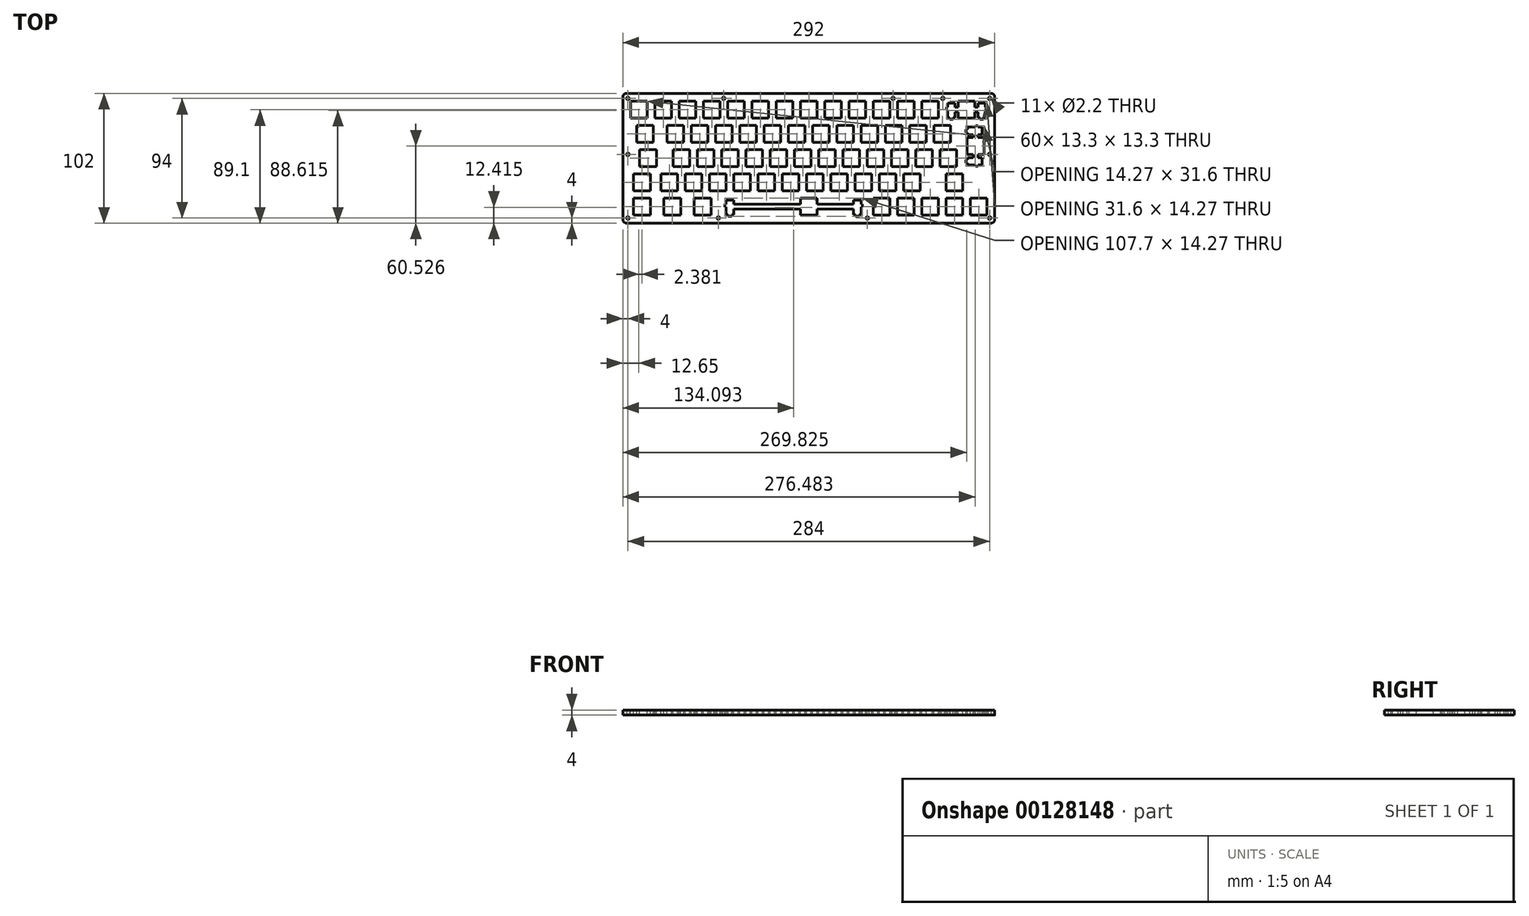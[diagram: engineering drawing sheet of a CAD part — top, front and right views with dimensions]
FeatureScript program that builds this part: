
annotation { "Feature Type Name" : "Feature", "Feature Type Description" : "" }
export const myFeature = defineFeature(function(context is Context, id is Id, definition is map)
    precondition{}
    {
        {
            var Q0;
            Q0=qCreatedBy(makeId("Top.planeOp"),FACE);
            var sketch = newSketch(context, id + "F0", { "sketchPlane" : qUnion([Q0])});
            skLineSegment(sketch, "E0.bottom", {"start": v(-143, 51) * mm, "end": v(143, 51) * mm});
            skLineSegment(sketch, "E0.top", {"start": v(-143, -51) * mm, "end": v(143, -51) * mm});
            skLineSegment(sketch, "E0.left", {"start": v(-146, 48) * mm, "end": v(-146, -48) * mm});
            skLineSegment(sketch, "E0.right", {"start": v(146, 48) * mm, "end": v(146, -48) * mm});
            skPoint(sketch, "E0.middle", {"position": v(0, 0) * mm});
            skPoint(sketch, "E1.visualSharp", {"position": v(-146, 51) * mm});
            skArc(sketch, "E1.filletArc", {"start": v(-143, 51) * mm, "mid": v(-145.12, 50.12) * mm, "end": v(-146, 48) * mm});
            skPoint(sketch, "E2.visualSharp", {"position": v(-146, -51) * mm});
            skArc(sketch, "E2.filletArc", {"start": v(-146, -48) * mm, "mid": v(-145.12, -50.12) * mm, "end": v(-143, -51) * mm});
            skPoint(sketch, "E3.visualSharp", {"position": v(146, 51) * mm});
            skArc(sketch, "E3.filletArc", {"start": v(146, 48) * mm, "mid": v(145.12, 50.12) * mm, "end": v(143, 51) * mm});
            skPoint(sketch, "E4.visualSharp", {"position": v(146, -51) * mm});
            skArc(sketch, "E4.filletArc", {"start": v(143, -51) * mm, "mid": v(145.12, -50.12) * mm, "end": v(146, -48) * mm});
            skCircle(sketch, "E5", {"center": v(-142, 47) * mm, "radius": 1.1 * mm});
            skCircle(sketch, "E6", {"center": v(-66.83, 47) * mm, "radius": 1.1 * mm});
            skCircle(sketch, "E7", {"center": v(66.17, 47) * mm, "radius": 1.1 * mm});
            skCircle(sketch, "E8", {"center": v(105.17, 47) * mm, "radius": 1.1 * mm});
            skCircle(sketch, "E9", {"center": v(142, 47) * mm, "radius": 1.1 * mm});
            skCircle(sketch, "E10", {"center": v(-142, -47) * mm, "radius": 1.1 * mm});
            skCircle(sketch, "E11", {"center": v(142, -47) * mm, "radius": 1.1 * mm});
            skCircle(sketch, "E12", {"center": v(-71, -47) * mm, "radius": 1.1 * mm});
            skCircle(sketch, "E13", {"center": v(46, -47) * mm, "radius": 1.1 * mm});
            skCircle(sketch, "E14", {"center": v(-142, 3) * mm, "radius": 1.1 * mm});
            skCircle(sketch, "E15", {"center": v(142, 3) * mm, "radius": 1.1 * mm});
            skSolve(sketch);
        }
        {
            var Q0;
            Q0=qSketchRegion(id+"F0",true);
            extrude(context, id + "F1", {"entities" : qUnion([Q0]), "depth" : 4 * mm});
        }
        {
            var Q0;
            Q0=makeQuery(id+"F1.opExtrude","CAP_FACE",FACE,{"disambiguationData":[OSD([sQuery(id+"F0.wireOp",EDGE,"E0.bottom"),sQuery(id+"F0.wireOp",EDGE,"E0.top"),sQuery(id+"F0.wireOp",EDGE,"E0.left"),sQuery(id+"F0.wireOp",EDGE,"E0.right"),sQuery(id+"F0.wireOp",EDGE,"E1.filletArc"),sQuery(id+"F0.wireOp",EDGE,"E2.filletArc"),sQuery(id+"F0.wireOp",EDGE,"E3.filletArc"),sQuery(id+"F0.wireOp",EDGE,"E4.filletArc"),sQuery(id+"F0.wireOp",EDGE,"E5"),sQuery(id+"F0.wireOp",EDGE,"E6"),sQuery(id+"F0.wireOp",EDGE,"E7"),sQuery(id+"F0.wireOp",EDGE,"E8"),sQuery(id+"F0.wireOp",EDGE,"E9"),sQuery(id+"F0.wireOp",EDGE,"E10"),sQuery(id+"F0.wireOp",EDGE,"E11"),sQuery(id+"F0.wireOp",EDGE,"E12"),sQuery(id+"F0.wireOp",EDGE,"E13"),sQuery(id+"F0.wireOp",EDGE,"E14"),sQuery(id+"F0.wireOp",EDGE,"E15")])],"isStart":false});
            var sketch = newSketch(context, id + "F2", { "sketchPlane" : qUnion([Q0])});
            skLineSegment(sketch, "E16", {"start": v(-18.56, -36.15) * mm, "end": v(-58.93, -36.15) * mm});
            skLineSegment(sketch, "E17", {"start": v(-58.93, -36.15) * mm, "end": v(-58.93, -32.92) * mm});
            skLineSegment(sketch, "E18", {"start": v(-58.93, -32.92) * mm, "end": v(-64.88, -32.92) * mm});
            skLineSegment(sketch, "E19", {"start": v(-64.88, -32.92) * mm, "end": v(-64.88, -36.15) * mm});
            skLineSegment(sketch, "E20", {"start": v(-64.88, -36.15) * mm, "end": v(-65.76, -36.15) * mm});
            skLineSegment(sketch, "E21", {"start": v(-65.76, -36.15) * mm, "end": v(-65.76, -38.25) * mm});
            skLineSegment(sketch, "E22", {"start": v(-65.76, -38.25) * mm, "end": v(-64.88, -38.25) * mm});
            skLineSegment(sketch, "E23", {"start": v(-64.88, -38.25) * mm, "end": v(-64.88, -44.52) * mm});
            skLineSegment(sketch, "E24", {"start": v(-64.88, -44.52) * mm, "end": v(-63.2, -44.52) * mm});
            skLineSegment(sketch, "E25", {"start": v(-63.2, -44.52) * mm, "end": v(-63.2, -45.72) * mm});
            skLineSegment(sketch, "E26", {"start": v(-63.2, -45.72) * mm, "end": v(-60.6, -45.72) * mm});
            skLineSegment(sketch, "E27", {"start": v(-60.6, -45.72) * mm, "end": v(-60.6, -44.52) * mm});
            skLineSegment(sketch, "E28", {"start": v(-60.6, -44.52) * mm, "end": v(-58.93, -44.52) * mm});
            skLineSegment(sketch, "E29", {"start": v(-58.93, -44.52) * mm, "end": v(-58.93, -40.05) * mm});
            skLineSegment(sketch, "E30", {"start": v(-58.93, -40.05) * mm, "end": v(-18.56, -40.05) * mm});
            skLineSegment(sketch, "E31", {"start": v(6.65, -40.05) * mm, "end": v(35.12, -40.05) * mm});
            skLineSegment(sketch, "E32", {"start": v(35.12, -40.05) * mm, "end": v(35.12, -44.52) * mm});
            skLineSegment(sketch, "E33", {"start": v(35.12, -44.52) * mm, "end": v(36.8, -44.52) * mm});
            skLineSegment(sketch, "E34", {"start": v(36.8, -44.52) * mm, "end": v(36.8, -45.72) * mm});
            skLineSegment(sketch, "E35", {"start": v(36.8, -45.72) * mm, "end": v(39.4, -45.72) * mm});
            skLineSegment(sketch, "E36", {"start": v(39.4, -45.72) * mm, "end": v(39.4, -44.52) * mm});
            skLineSegment(sketch, "E37", {"start": v(39.4, -44.52) * mm, "end": v(41.07, -44.52) * mm});
            skLineSegment(sketch, "E38", {"start": v(41.07, -44.52) * mm, "end": v(41.07, -38.25) * mm});
            skLineSegment(sketch, "E39", {"start": v(41.07, -38.25) * mm, "end": v(41.94, -38.25) * mm});
            skLineSegment(sketch, "E40", {"start": v(41.94, -38.25) * mm, "end": v(41.94, -36.15) * mm});
            skLineSegment(sketch, "E41", {"start": v(41.94, -36.15) * mm, "end": v(41.07, -36.15) * mm});
            skLineSegment(sketch, "E42", {"start": v(41.07, -36.15) * mm, "end": v(41.07, -32.92) * mm});
            skLineSegment(sketch, "E43", {"start": v(41.07, -32.92) * mm, "end": v(35.12, -32.92) * mm});
            skLineSegment(sketch, "E44", {"start": v(35.12, -32.92) * mm, "end": v(35.12, -36.15) * mm});
            skLineSegment(sketch, "E45", {"start": v(35.12, -36.15) * mm, "end": v(6.65, -36.15) * mm});
            skLineSegment(sketch, "E46", {"start": v(-5.26, -31.45) * mm, "end": v(-6.65, -31.45) * mm});
            skLineSegment(sketch, "E47", {"start": v(-137.62, -31.45) * mm, "end": v(-124.32, -31.45) * mm});
            skLineSegment(sketch, "E48", {"start": v(-124.32, -31.45) * mm, "end": v(-124.32, -44.75) * mm});
            skLineSegment(sketch, "E49", {"start": v(-124.32, -44.75) * mm, "end": v(-137.62, -44.75) * mm});
            skLineSegment(sketch, "E50", {"start": v(-137.62, -44.75) * mm, "end": v(-137.62, -31.45) * mm});
            skLineSegment(sketch, "E51", {"start": v(-113.8, -31.45) * mm, "end": v(-100.5, -31.45) * mm});
            skLineSegment(sketch, "E52", {"start": v(-100.5, -31.45) * mm, "end": v(-100.5, -44.75) * mm});
            skLineSegment(sketch, "E53", {"start": v(-100.5, -44.75) * mm, "end": v(-113.8, -44.75) * mm});
            skLineSegment(sketch, "E54", {"start": v(-113.8, -44.75) * mm, "end": v(-113.8, -31.45) * mm});
            skLineSegment(sketch, "E55", {"start": v(-90, -31.45) * mm, "end": v(-76.7, -31.45) * mm});
            skLineSegment(sketch, "E56", {"start": v(-76.7, -31.45) * mm, "end": v(-76.7, -44.75) * mm});
            skLineSegment(sketch, "E57", {"start": v(-76.7, -44.75) * mm, "end": v(-90, -44.75) * mm});
            skLineSegment(sketch, "E58", {"start": v(-90, -44.75) * mm, "end": v(-90, -31.45) * mm});
            skLineSegment(sketch, "E59", {"start": v(50.5, -31.45) * mm, "end": v(63.8, -31.45) * mm});
            skLineSegment(sketch, "E60", {"start": v(63.8, -31.45) * mm, "end": v(63.8, -44.75) * mm});
            skLineSegment(sketch, "E61", {"start": v(63.8, -44.75) * mm, "end": v(50.5, -44.75) * mm});
            skLineSegment(sketch, "E62", {"start": v(50.5, -44.75) * mm, "end": v(50.5, -31.45) * mm});
            skLineSegment(sketch, "E63", {"start": v(69.55, -31.45) * mm, "end": v(82.85, -31.45) * mm});
            skLineSegment(sketch, "E64", {"start": v(82.85, -31.45) * mm, "end": v(82.85, -44.75) * mm});
            skLineSegment(sketch, "E65", {"start": v(82.85, -44.75) * mm, "end": v(69.55, -44.75) * mm});
            skLineSegment(sketch, "E66", {"start": v(69.55, -44.75) * mm, "end": v(69.55, -31.45) * mm});
            skLineSegment(sketch, "E67", {"start": v(88.6, -31.45) * mm, "end": v(101.9, -31.45) * mm});
            skLineSegment(sketch, "E68", {"start": v(101.9, -31.45) * mm, "end": v(101.9, -44.75) * mm});
            skLineSegment(sketch, "E69", {"start": v(101.9, -44.75) * mm, "end": v(88.6, -44.75) * mm});
            skLineSegment(sketch, "E70", {"start": v(88.6, -44.75) * mm, "end": v(88.6, -31.45) * mm});
            skLineSegment(sketch, "E71", {"start": v(107.65, -31.45) * mm, "end": v(120.95, -31.45) * mm});
            skLineSegment(sketch, "E72", {"start": v(120.95, -31.45) * mm, "end": v(120.95, -44.75) * mm});
            skLineSegment(sketch, "E73", {"start": v(120.95, -44.75) * mm, "end": v(107.65, -44.75) * mm});
            skLineSegment(sketch, "E74", {"start": v(107.65, -44.75) * mm, "end": v(107.65, -31.45) * mm});
            skLineSegment(sketch, "E75", {"start": v(126.7, -31.45) * mm, "end": v(140, -31.45) * mm});
            skLineSegment(sketch, "E76", {"start": v(140, -31.45) * mm, "end": v(140, -44.75) * mm});
            skLineSegment(sketch, "E77", {"start": v(140, -44.75) * mm, "end": v(126.7, -44.75) * mm});
            skLineSegment(sketch, "E78", {"start": v(126.7, -44.75) * mm, "end": v(126.7, -31.45) * mm});
            skLineSegment(sketch, "E79", {"start": v(-137.62, -12.4) * mm, "end": v(-124.32, -12.4) * mm});
            skLineSegment(sketch, "E80", {"start": v(-124.32, -12.4) * mm, "end": v(-124.32, -25.7) * mm});
            skLineSegment(sketch, "E81", {"start": v(-124.32, -25.7) * mm, "end": v(-137.62, -25.7) * mm});
            skLineSegment(sketch, "E82", {"start": v(-137.62, -25.7) * mm, "end": v(-137.62, -12.4) * mm});
            skLineSegment(sketch, "E83", {"start": v(-116.19, -12.4) * mm, "end": v(-102.89, -12.4) * mm});
            skLineSegment(sketch, "E84", {"start": v(-102.89, -12.4) * mm, "end": v(-102.89, -25.7) * mm});
            skLineSegment(sketch, "E85", {"start": v(-102.89, -25.7) * mm, "end": v(-116.19, -25.7) * mm});
            skLineSegment(sketch, "E86", {"start": v(-116.19, -25.7) * mm, "end": v(-116.19, -12.4) * mm});
            skLineSegment(sketch, "E87", {"start": v(-97.14, -12.4) * mm, "end": v(-83.84, -12.4) * mm});
            skLineSegment(sketch, "E88", {"start": v(-83.84, -12.4) * mm, "end": v(-83.84, -25.7) * mm});
            skLineSegment(sketch, "E89", {"start": v(-83.84, -25.7) * mm, "end": v(-97.14, -25.7) * mm});
            skLineSegment(sketch, "E90", {"start": v(-97.14, -25.7) * mm, "end": v(-97.14, -12.4) * mm});
            skLineSegment(sketch, "E91", {"start": v(-78.09, -12.4) * mm, "end": v(-64.79, -12.4) * mm});
            skLineSegment(sketch, "E92", {"start": v(-64.79, -12.4) * mm, "end": v(-64.79, -25.7) * mm});
            skLineSegment(sketch, "E93", {"start": v(-64.79, -25.7) * mm, "end": v(-78.09, -25.7) * mm});
            skLineSegment(sketch, "E94", {"start": v(-78.09, -25.7) * mm, "end": v(-78.09, -12.4) * mm});
            skLineSegment(sketch, "E95", {"start": v(-59.04, -12.4) * mm, "end": v(-45.74, -12.4) * mm});
            skLineSegment(sketch, "E96", {"start": v(-45.74, -12.4) * mm, "end": v(-45.74, -25.7) * mm});
            skLineSegment(sketch, "E97", {"start": v(-45.74, -25.7) * mm, "end": v(-59.04, -25.7) * mm});
            skLineSegment(sketch, "E98", {"start": v(-59.04, -25.7) * mm, "end": v(-59.04, -12.4) * mm});
            skLineSegment(sketch, "E99", {"start": v(-39.99, -12.4) * mm, "end": v(-26.69, -12.4) * mm});
            skLineSegment(sketch, "E100", {"start": v(-26.69, -12.4) * mm, "end": v(-26.69, -25.7) * mm});
            skLineSegment(sketch, "E101", {"start": v(-26.69, -25.7) * mm, "end": v(-39.99, -25.7) * mm});
            skLineSegment(sketch, "E102", {"start": v(-39.99, -25.7) * mm, "end": v(-39.99, -12.4) * mm});
            skLineSegment(sketch, "E103", {"start": v(-20.94, -12.4) * mm, "end": v(-7.64, -12.4) * mm});
            skLineSegment(sketch, "E104", {"start": v(-7.64, -12.4) * mm, "end": v(-7.64, -25.7) * mm});
            skLineSegment(sketch, "E105", {"start": v(-7.64, -25.7) * mm, "end": v(-20.94, -25.7) * mm});
            skLineSegment(sketch, "E106", {"start": v(-20.94, -25.7) * mm, "end": v(-20.94, -12.4) * mm});
            skLineSegment(sketch, "E107", {"start": v(-1.89, -12.4) * mm, "end": v(11.41, -12.4) * mm});
            skLineSegment(sketch, "E108", {"start": v(11.41, -12.4) * mm, "end": v(11.41, -25.7) * mm});
            skLineSegment(sketch, "E109", {"start": v(11.41, -25.7) * mm, "end": v(-1.89, -25.7) * mm});
            skLineSegment(sketch, "E110", {"start": v(-1.89, -25.7) * mm, "end": v(-1.89, -12.4) * mm});
            skLineSegment(sketch, "E111", {"start": v(17.16, -12.4) * mm, "end": v(30.46, -12.4) * mm});
            skLineSegment(sketch, "E112", {"start": v(30.46, -12.4) * mm, "end": v(30.46, -25.7) * mm});
            skLineSegment(sketch, "E113", {"start": v(30.46, -25.7) * mm, "end": v(17.16, -25.7) * mm});
            skLineSegment(sketch, "E114", {"start": v(17.16, -25.7) * mm, "end": v(17.16, -12.4) * mm});
            skLineSegment(sketch, "E115", {"start": v(36.21, -12.4) * mm, "end": v(49.51, -12.4) * mm});
            skLineSegment(sketch, "E116", {"start": v(49.51, -12.4) * mm, "end": v(49.51, -25.7) * mm});
            skLineSegment(sketch, "E117", {"start": v(49.51, -25.7) * mm, "end": v(36.21, -25.7) * mm});
            skLineSegment(sketch, "E118", {"start": v(36.21, -25.7) * mm, "end": v(36.21, -12.4) * mm});
            skLineSegment(sketch, "E119", {"start": v(55.26, -12.4) * mm, "end": v(68.56, -12.4) * mm});
            skLineSegment(sketch, "E120", {"start": v(68.56, -12.4) * mm, "end": v(68.56, -25.7) * mm});
            skLineSegment(sketch, "E121", {"start": v(68.56, -25.7) * mm, "end": v(55.26, -25.7) * mm});
            skLineSegment(sketch, "E122", {"start": v(55.26, -25.7) * mm, "end": v(55.26, -12.4) * mm});
            skLineSegment(sketch, "E123", {"start": v(74.31, -12.4) * mm, "end": v(87.61, -12.4) * mm});
            skLineSegment(sketch, "E124", {"start": v(87.61, -12.4) * mm, "end": v(87.61, -25.7) * mm});
            skLineSegment(sketch, "E125", {"start": v(87.61, -25.7) * mm, "end": v(74.31, -25.7) * mm});
            skLineSegment(sketch, "E126", {"start": v(74.31, -25.7) * mm, "end": v(74.31, -12.4) * mm});
            skLineSegment(sketch, "E127", {"start": v(107.65, -12.4) * mm, "end": v(120.95, -12.4) * mm});
            skLineSegment(sketch, "E128", {"start": v(120.95, -12.4) * mm, "end": v(120.95, -25.7) * mm});
            skLineSegment(sketch, "E129", {"start": v(120.95, -25.7) * mm, "end": v(107.65, -25.7) * mm});
            skLineSegment(sketch, "E130", {"start": v(107.65, -25.7) * mm, "end": v(107.65, -12.4) * mm});
            skLineSegment(sketch, "E131", {"start": v(-132.86, 6.65) * mm, "end": v(-119.56, 6.65) * mm});
            skLineSegment(sketch, "E132", {"start": v(-119.56, 6.65) * mm, "end": v(-119.56, -6.65) * mm});
            skLineSegment(sketch, "E133", {"start": v(-119.56, -6.65) * mm, "end": v(-132.86, -6.65) * mm});
            skLineSegment(sketch, "E134", {"start": v(-132.86, -6.65) * mm, "end": v(-132.86, 6.65) * mm});
            skLineSegment(sketch, "E135", {"start": v(-106.66, 6.65) * mm, "end": v(-93.36, 6.65) * mm});
            skLineSegment(sketch, "E136", {"start": v(-93.36, 6.65) * mm, "end": v(-93.36, -6.65) * mm});
            skLineSegment(sketch, "E137", {"start": v(-93.36, -6.65) * mm, "end": v(-106.66, -6.65) * mm});
            skLineSegment(sketch, "E138", {"start": v(-106.66, -6.65) * mm, "end": v(-106.66, 6.65) * mm});
            skLineSegment(sketch, "E139", {"start": v(-87.61, 6.65) * mm, "end": v(-74.31, 6.65) * mm});
            skLineSegment(sketch, "E140", {"start": v(-74.31, 6.65) * mm, "end": v(-74.31, -6.65) * mm});
            skLineSegment(sketch, "E141", {"start": v(-74.31, -6.65) * mm, "end": v(-87.61, -6.65) * mm});
            skLineSegment(sketch, "E142", {"start": v(-87.61, -6.65) * mm, "end": v(-87.61, 6.65) * mm});
            skLineSegment(sketch, "E143", {"start": v(-68.56, 6.65) * mm, "end": v(-55.26, 6.65) * mm});
            skLineSegment(sketch, "E144", {"start": v(-55.26, 6.65) * mm, "end": v(-55.26, -6.65) * mm});
            skLineSegment(sketch, "E145", {"start": v(-55.26, -6.65) * mm, "end": v(-68.56, -6.65) * mm});
            skLineSegment(sketch, "E146", {"start": v(-68.56, -6.65) * mm, "end": v(-68.56, 6.65) * mm});
            skLineSegment(sketch, "E147", {"start": v(-49.51, 6.65) * mm, "end": v(-36.21, 6.65) * mm});
            skLineSegment(sketch, "E148", {"start": v(-36.21, 6.65) * mm, "end": v(-36.21, -6.65) * mm});
            skLineSegment(sketch, "E149", {"start": v(-36.21, -6.65) * mm, "end": v(-49.51, -6.65) * mm});
            skLineSegment(sketch, "E150", {"start": v(-49.51, -6.65) * mm, "end": v(-49.51, 6.65) * mm});
            skLineSegment(sketch, "E151", {"start": v(-30.46, 6.65) * mm, "end": v(-17.16, 6.65) * mm});
            skLineSegment(sketch, "E152", {"start": v(-17.16, 6.65) * mm, "end": v(-17.16, -6.65) * mm});
            skLineSegment(sketch, "E153", {"start": v(-17.16, -6.65) * mm, "end": v(-30.46, -6.65) * mm});
            skLineSegment(sketch, "E154", {"start": v(-30.46, -6.65) * mm, "end": v(-30.46, 6.65) * mm});
            skLineSegment(sketch, "E155", {"start": v(-11.41, 6.65) * mm, "end": v(1.89, 6.65) * mm});
            skLineSegment(sketch, "E156", {"start": v(1.89, 6.65) * mm, "end": v(1.89, -6.65) * mm});
            skLineSegment(sketch, "E157", {"start": v(1.89, -6.65) * mm, "end": v(-11.41, -6.65) * mm});
            skLineSegment(sketch, "E158", {"start": v(-11.41, -6.65) * mm, "end": v(-11.41, 6.65) * mm});
            skLineSegment(sketch, "E159", {"start": v(7.64, 6.65) * mm, "end": v(20.94, 6.65) * mm});
            skLineSegment(sketch, "E160", {"start": v(20.94, 6.65) * mm, "end": v(20.94, -6.65) * mm});
            skLineSegment(sketch, "E161", {"start": v(20.94, -6.65) * mm, "end": v(7.64, -6.65) * mm});
            skLineSegment(sketch, "E162", {"start": v(7.64, -6.65) * mm, "end": v(7.64, 6.65) * mm});
            skLineSegment(sketch, "E163", {"start": v(26.69, 6.65) * mm, "end": v(39.99, 6.65) * mm});
            skLineSegment(sketch, "E164", {"start": v(39.99, 6.65) * mm, "end": v(39.99, -6.65) * mm});
            skLineSegment(sketch, "E165", {"start": v(39.99, -6.65) * mm, "end": v(26.69, -6.65) * mm});
            skLineSegment(sketch, "E166", {"start": v(26.69, -6.65) * mm, "end": v(26.69, 6.65) * mm});
            skLineSegment(sketch, "E167", {"start": v(45.74, 6.65) * mm, "end": v(59.04, 6.65) * mm});
            skLineSegment(sketch, "E168", {"start": v(59.04, 6.65) * mm, "end": v(59.04, -6.65) * mm});
            skLineSegment(sketch, "E169", {"start": v(59.04, -6.65) * mm, "end": v(45.74, -6.65) * mm});
            skLineSegment(sketch, "E170", {"start": v(45.74, -6.65) * mm, "end": v(45.74, 6.65) * mm});
            skLineSegment(sketch, "E171", {"start": v(64.79, 6.65) * mm, "end": v(78.09, 6.65) * mm});
            skLineSegment(sketch, "E172", {"start": v(78.09, 6.65) * mm, "end": v(78.09, -6.65) * mm});
            skLineSegment(sketch, "E173", {"start": v(78.09, -6.65) * mm, "end": v(64.79, -6.65) * mm});
            skLineSegment(sketch, "E174", {"start": v(64.79, -6.65) * mm, "end": v(64.79, 6.65) * mm});
            skLineSegment(sketch, "E175", {"start": v(83.84, 6.65) * mm, "end": v(97.14, 6.65) * mm});
            skLineSegment(sketch, "E176", {"start": v(97.14, 6.65) * mm, "end": v(97.14, -6.65) * mm});
            skLineSegment(sketch, "E177", {"start": v(97.14, -6.65) * mm, "end": v(83.84, -6.65) * mm});
            skLineSegment(sketch, "E178", {"start": v(83.84, -6.65) * mm, "end": v(83.84, 6.65) * mm});
            skLineSegment(sketch, "E179", {"start": v(102.89, 6.65) * mm, "end": v(116.19, 6.65) * mm});
            skLineSegment(sketch, "E180", {"start": v(116.19, 6.65) * mm, "end": v(116.19, -6.65) * mm});
            skLineSegment(sketch, "E181", {"start": v(116.19, -6.65) * mm, "end": v(102.89, -6.65) * mm});
            skLineSegment(sketch, "E182", {"start": v(102.89, -6.65) * mm, "end": v(102.89, 6.65) * mm});
            skLineSegment(sketch, "E183", {"start": v(130.82, 25.33) * mm, "end": v(130.82, 24.45) * mm});
            skLineSegment(sketch, "E184", {"start": v(130.82, 24.45) * mm, "end": v(124.55, 24.45) * mm});
            skLineSegment(sketch, "E185", {"start": v(124.55, 24.45) * mm, "end": v(124.55, 22.78) * mm});
            skLineSegment(sketch, "E186", {"start": v(124.55, 22.78) * mm, "end": v(123.35, 22.78) * mm});
            skLineSegment(sketch, "E187", {"start": v(123.35, 22.78) * mm, "end": v(123.35, 20.17) * mm});
            skLineSegment(sketch, "E188", {"start": v(123.35, 20.17) * mm, "end": v(124.55, 20.17) * mm});
            skLineSegment(sketch, "E189", {"start": v(124.55, 20.17) * mm, "end": v(124.55, 18.5) * mm});
            skLineSegment(sketch, "E190", {"start": v(124.55, 18.5) * mm, "end": v(129.02, 18.5) * mm});
            skLineSegment(sketch, "E191", {"start": v(129.02, 18.5) * mm, "end": v(129.02, 16.18) * mm});
            skLineSegment(sketch, "E192", {"start": v(129.02, 16.18) * mm, "end": v(124.32, 16.18) * mm});
            skLineSegment(sketch, "E193", {"start": v(124.32, 16.18) * mm, "end": v(124.32, 2.88) * mm});
            skLineSegment(sketch, "E194", {"start": v(124.32, 2.88) * mm, "end": v(129.02, 2.88) * mm});
            skLineSegment(sketch, "E195", {"start": v(129.02, 2.88) * mm, "end": v(129.02, 0.55) * mm});
            skLineSegment(sketch, "E196", {"start": v(129.02, 0.55) * mm, "end": v(124.55, 0.55) * mm});
            skLineSegment(sketch, "E197", {"start": v(124.55, 0.55) * mm, "end": v(124.55, -1.12) * mm});
            skLineSegment(sketch, "E198", {"start": v(124.55, -1.12) * mm, "end": v(123.35, -1.12) * mm});
            skLineSegment(sketch, "E199", {"start": v(123.35, -1.12) * mm, "end": v(123.35, -3.72) * mm});
            skLineSegment(sketch, "E200", {"start": v(123.35, -3.72) * mm, "end": v(124.55, -3.72) * mm});
            skLineSegment(sketch, "E201", {"start": v(124.55, -3.72) * mm, "end": v(124.55, -5.4) * mm});
            skLineSegment(sketch, "E202", {"start": v(124.55, -5.4) * mm, "end": v(130.82, -5.4) * mm});
            skLineSegment(sketch, "E203", {"start": v(130.82, -5.4) * mm, "end": v(130.82, -6.27) * mm});
            skLineSegment(sketch, "E204", {"start": v(130.82, -6.27) * mm, "end": v(132.92, -6.27) * mm});
            skLineSegment(sketch, "E205", {"start": v(132.92, -6.27) * mm, "end": v(132.92, -5.4) * mm});
            skLineSegment(sketch, "E206", {"start": v(132.92, -5.4) * mm, "end": v(136.15, -5.4) * mm});
            skLineSegment(sketch, "E207", {"start": v(136.15, -5.4) * mm, "end": v(136.15, 0.55) * mm});
            skLineSegment(sketch, "E208", {"start": v(136.15, 0.55) * mm, "end": v(132.92, 0.55) * mm});
            skLineSegment(sketch, "E209", {"start": v(132.92, 0.55) * mm, "end": v(132.92, 2.88) * mm});
            skLineSegment(sketch, "E210", {"start": v(132.92, 2.88) * mm, "end": v(137.62, 2.88) * mm});
            skLineSegment(sketch, "E211", {"start": v(137.62, 2.88) * mm, "end": v(137.62, 16.18) * mm});
            skLineSegment(sketch, "E212", {"start": v(137.62, 16.18) * mm, "end": v(132.92, 16.18) * mm});
            skLineSegment(sketch, "E213", {"start": v(132.92, 16.18) * mm, "end": v(132.92, 18.5) * mm});
            skLineSegment(sketch, "E214", {"start": v(132.92, 18.5) * mm, "end": v(136.15, 18.5) * mm});
            skLineSegment(sketch, "E215", {"start": v(136.15, 18.5) * mm, "end": v(136.15, 24.45) * mm});
            skLineSegment(sketch, "E216", {"start": v(136.15, 24.45) * mm, "end": v(132.92, 24.45) * mm});
            skLineSegment(sketch, "E217", {"start": v(132.92, 24.45) * mm, "end": v(132.92, 25.33) * mm});
            skLineSegment(sketch, "E218", {"start": v(132.92, 25.33) * mm, "end": v(130.82, 25.33) * mm});
            skLineSegment(sketch, "E219", {"start": v(-135.24, 25.7) * mm, "end": v(-121.94, 25.7) * mm});
            skLineSegment(sketch, "E220", {"start": v(-121.94, 25.7) * mm, "end": v(-121.94, 12.4) * mm});
            skLineSegment(sketch, "E221", {"start": v(-121.94, 12.4) * mm, "end": v(-135.24, 12.4) * mm});
            skLineSegment(sketch, "E222", {"start": v(-135.24, 12.4) * mm, "end": v(-135.24, 25.7) * mm});
            skLineSegment(sketch, "E223", {"start": v(-111.43, 25.7) * mm, "end": v(-98.12, 25.7) * mm});
            skLineSegment(sketch, "E224", {"start": v(-98.12, 25.7) * mm, "end": v(-98.12, 12.4) * mm});
            skLineSegment(sketch, "E225", {"start": v(-98.12, 12.4) * mm, "end": v(-111.43, 12.4) * mm});
            skLineSegment(sketch, "E226", {"start": v(-111.43, 12.4) * mm, "end": v(-111.43, 25.7) * mm});
            skLineSegment(sketch, "E227", {"start": v(-92.38, 25.7) * mm, "end": v(-79.07, 25.7) * mm});
            skLineSegment(sketch, "E228", {"start": v(-79.07, 25.7) * mm, "end": v(-79.07, 12.4) * mm});
            skLineSegment(sketch, "E229", {"start": v(-79.07, 12.4) * mm, "end": v(-92.38, 12.4) * mm});
            skLineSegment(sketch, "E230", {"start": v(-92.38, 12.4) * mm, "end": v(-92.38, 25.7) * mm});
            skLineSegment(sketch, "E231", {"start": v(-73.33, 25.7) * mm, "end": v(-60.02, 25.7) * mm});
            skLineSegment(sketch, "E232", {"start": v(-60.02, 25.7) * mm, "end": v(-60.02, 12.4) * mm});
            skLineSegment(sketch, "E233", {"start": v(-60.02, 12.4) * mm, "end": v(-73.33, 12.4) * mm});
            skLineSegment(sketch, "E234", {"start": v(-73.33, 12.4) * mm, "end": v(-73.33, 25.7) * mm});
            skLineSegment(sketch, "E235", {"start": v(-54.28, 25.7) * mm, "end": v(-40.97, 25.7) * mm});
            skLineSegment(sketch, "E236", {"start": v(-40.97, 25.7) * mm, "end": v(-40.97, 12.4) * mm});
            skLineSegment(sketch, "E237", {"start": v(-40.97, 12.4) * mm, "end": v(-54.28, 12.4) * mm});
            skLineSegment(sketch, "E238", {"start": v(-54.28, 12.4) * mm, "end": v(-54.28, 25.7) * mm});
            skLineSegment(sketch, "E239", {"start": v(-35.23, 25.7) * mm, "end": v(-21.92, 25.7) * mm});
            skLineSegment(sketch, "E240", {"start": v(-21.92, 25.7) * mm, "end": v(-21.92, 12.4) * mm});
            skLineSegment(sketch, "E241", {"start": v(-21.92, 12.4) * mm, "end": v(-35.23, 12.4) * mm});
            skLineSegment(sketch, "E242", {"start": v(-35.23, 12.4) * mm, "end": v(-35.23, 25.7) * mm});
            skLineSegment(sketch, "E243", {"start": v(-16.18, 25.7) * mm, "end": v(-2.87, 25.7) * mm});
            skLineSegment(sketch, "E244", {"start": v(-2.87, 25.7) * mm, "end": v(-2.87, 12.4) * mm});
            skLineSegment(sketch, "E245", {"start": v(-2.87, 12.4) * mm, "end": v(-16.18, 12.4) * mm});
            skLineSegment(sketch, "E246", {"start": v(-16.18, 12.4) * mm, "end": v(-16.18, 25.7) * mm});
            skLineSegment(sketch, "E247", {"start": v(2.87, 25.7) * mm, "end": v(16.18, 25.7) * mm});
            skLineSegment(sketch, "E248", {"start": v(16.18, 25.7) * mm, "end": v(16.18, 12.4) * mm});
            skLineSegment(sketch, "E249", {"start": v(16.18, 12.4) * mm, "end": v(2.87, 12.4) * mm});
            skLineSegment(sketch, "E250", {"start": v(2.87, 12.4) * mm, "end": v(2.87, 25.7) * mm});
            skLineSegment(sketch, "E251", {"start": v(21.92, 25.7) * mm, "end": v(35.23, 25.7) * mm});
            skLineSegment(sketch, "E252", {"start": v(35.23, 25.7) * mm, "end": v(35.23, 12.4) * mm});
            skLineSegment(sketch, "E253", {"start": v(35.23, 12.4) * mm, "end": v(21.92, 12.4) * mm});
            skLineSegment(sketch, "E254", {"start": v(21.92, 12.4) * mm, "end": v(21.92, 25.7) * mm});
            skLineSegment(sketch, "E255", {"start": v(40.97, 25.7) * mm, "end": v(54.28, 25.7) * mm});
            skLineSegment(sketch, "E256", {"start": v(54.28, 25.7) * mm, "end": v(54.28, 12.4) * mm});
            skLineSegment(sketch, "E257", {"start": v(54.28, 12.4) * mm, "end": v(40.97, 12.4) * mm});
            skLineSegment(sketch, "E258", {"start": v(40.97, 12.4) * mm, "end": v(40.97, 25.7) * mm});
            skLineSegment(sketch, "E259", {"start": v(60.02, 25.7) * mm, "end": v(73.33, 25.7) * mm});
            skLineSegment(sketch, "E260", {"start": v(73.33, 25.7) * mm, "end": v(73.33, 12.4) * mm});
            skLineSegment(sketch, "E261", {"start": v(73.33, 12.4) * mm, "end": v(60.02, 12.4) * mm});
            skLineSegment(sketch, "E262", {"start": v(60.02, 12.4) * mm, "end": v(60.02, 25.7) * mm});
            skLineSegment(sketch, "E263", {"start": v(79.07, 25.7) * mm, "end": v(92.38, 25.7) * mm});
            skLineSegment(sketch, "E264", {"start": v(92.38, 25.7) * mm, "end": v(92.38, 12.4) * mm});
            skLineSegment(sketch, "E265", {"start": v(92.38, 12.4) * mm, "end": v(79.07, 12.4) * mm});
            skLineSegment(sketch, "E266", {"start": v(79.07, 12.4) * mm, "end": v(79.07, 25.7) * mm});
            skLineSegment(sketch, "E267", {"start": v(98.12, 25.7) * mm, "end": v(111.42, 25.7) * mm});
            skLineSegment(sketch, "E268", {"start": v(111.42, 25.7) * mm, "end": v(111.42, 12.4) * mm});
            skLineSegment(sketch, "E269", {"start": v(111.42, 12.4) * mm, "end": v(98.12, 12.4) * mm});
            skLineSegment(sketch, "E270", {"start": v(98.12, 12.4) * mm, "end": v(98.12, 25.7) * mm});
            skLineSegment(sketch, "E271", {"start": v(117.17, 44.75) * mm, "end": v(117.17, 40.05) * mm});
            skLineSegment(sketch, "E272", {"start": v(117.17, 40.05) * mm, "end": v(114.85, 40.05) * mm});
            skLineSegment(sketch, "E273", {"start": v(114.85, 40.05) * mm, "end": v(114.85, 43.28) * mm});
            skLineSegment(sketch, "E274", {"start": v(114.85, 43.28) * mm, "end": v(108.9, 43.28) * mm});
            skLineSegment(sketch, "E275", {"start": v(108.9, 43.28) * mm, "end": v(108.9, 40.05) * mm});
            skLineSegment(sketch, "E276", {"start": v(108.9, 40.05) * mm, "end": v(108.02, 40.05) * mm});
            skLineSegment(sketch, "E277", {"start": v(108.02, 40.05) * mm, "end": v(108.02, 37.95) * mm});
            skLineSegment(sketch, "E278", {"start": v(108.02, 37.95) * mm, "end": v(108.9, 37.95) * mm});
            skLineSegment(sketch, "E279", {"start": v(108.9, 37.95) * mm, "end": v(108.9, 31.68) * mm});
            skLineSegment(sketch, "E280", {"start": v(108.9, 31.68) * mm, "end": v(110.58, 31.68) * mm});
            skLineSegment(sketch, "E281", {"start": v(110.58, 31.68) * mm, "end": v(110.58, 30.48) * mm});
            skLineSegment(sketch, "E282", {"start": v(110.58, 30.48) * mm, "end": v(113.17, 30.48) * mm});
            skLineSegment(sketch, "E283", {"start": v(113.17, 30.48) * mm, "end": v(113.17, 31.68) * mm});
            skLineSegment(sketch, "E284", {"start": v(113.17, 31.68) * mm, "end": v(114.85, 31.68) * mm});
            skLineSegment(sketch, "E285", {"start": v(114.85, 31.68) * mm, "end": v(114.85, 36.15) * mm});
            skLineSegment(sketch, "E286", {"start": v(114.85, 36.15) * mm, "end": v(117.17, 36.15) * mm});
            skLineSegment(sketch, "E287", {"start": v(117.17, 36.15) * mm, "end": v(117.17, 31.45) * mm});
            skLineSegment(sketch, "E288", {"start": v(117.17, 31.45) * mm, "end": v(130.48, 31.45) * mm});
            skLineSegment(sketch, "E289", {"start": v(130.48, 31.45) * mm, "end": v(130.48, 36.15) * mm});
            skLineSegment(sketch, "E290", {"start": v(130.48, 36.15) * mm, "end": v(132.8, 36.15) * mm});
            skLineSegment(sketch, "E291", {"start": v(132.8, 36.15) * mm, "end": v(132.8, 31.68) * mm});
            skLineSegment(sketch, "E292", {"start": v(132.8, 31.68) * mm, "end": v(134.47, 31.68) * mm});
            skLineSegment(sketch, "E293", {"start": v(134.47, 31.68) * mm, "end": v(134.47, 30.48) * mm});
            skLineSegment(sketch, "E294", {"start": v(134.47, 30.48) * mm, "end": v(137.07, 30.48) * mm});
            skLineSegment(sketch, "E295", {"start": v(137.07, 30.48) * mm, "end": v(137.07, 31.68) * mm});
            skLineSegment(sketch, "E296", {"start": v(137.07, 31.68) * mm, "end": v(138.75, 31.68) * mm});
            skLineSegment(sketch, "E297", {"start": v(138.75, 31.68) * mm, "end": v(138.75, 37.95) * mm});
            skLineSegment(sketch, "E298", {"start": v(138.75, 37.95) * mm, "end": v(139.63, 37.95) * mm});
            skLineSegment(sketch, "E299", {"start": v(139.63, 37.95) * mm, "end": v(139.63, 40.05) * mm});
            skLineSegment(sketch, "E300", {"start": v(139.63, 40.05) * mm, "end": v(138.75, 40.05) * mm});
            skLineSegment(sketch, "E301", {"start": v(138.75, 40.05) * mm, "end": v(138.75, 43.28) * mm});
            skLineSegment(sketch, "E302", {"start": v(138.75, 43.28) * mm, "end": v(132.8, 43.28) * mm});
            skLineSegment(sketch, "E303", {"start": v(132.8, 43.28) * mm, "end": v(132.8, 40.05) * mm});
            skLineSegment(sketch, "E304", {"start": v(132.8, 40.05) * mm, "end": v(130.48, 40.05) * mm});
            skLineSegment(sketch, "E305", {"start": v(130.48, 40.05) * mm, "end": v(130.48, 44.75) * mm});
            skLineSegment(sketch, "E306", {"start": v(130.48, 44.75) * mm, "end": v(117.17, 44.75) * mm});
            skLineSegment(sketch, "E307", {"start": v(-140, 44.75) * mm, "end": v(-126.7, 44.75) * mm});
            skLineSegment(sketch, "E308", {"start": v(-126.7, 44.75) * mm, "end": v(-126.7, 31.45) * mm});
            skLineSegment(sketch, "E309", {"start": v(-126.7, 31.45) * mm, "end": v(-140, 31.45) * mm});
            skLineSegment(sketch, "E310", {"start": v(-140, 31.45) * mm, "end": v(-140, 44.75) * mm});
            skLineSegment(sketch, "E311", {"start": v(-120.95, 44.75) * mm, "end": v(-107.65, 44.75) * mm});
            skLineSegment(sketch, "E312", {"start": v(-107.65, 44.75) * mm, "end": v(-107.65, 31.45) * mm});
            skLineSegment(sketch, "E313", {"start": v(-107.65, 31.45) * mm, "end": v(-120.95, 31.45) * mm});
            skLineSegment(sketch, "E314", {"start": v(-120.95, 31.45) * mm, "end": v(-120.95, 44.75) * mm});
            skLineSegment(sketch, "E315", {"start": v(-101.9, 44.75) * mm, "end": v(-88.6, 44.75) * mm});
            skLineSegment(sketch, "E316", {"start": v(-88.6, 44.75) * mm, "end": v(-88.6, 31.45) * mm});
            skLineSegment(sketch, "E317", {"start": v(-88.6, 31.45) * mm, "end": v(-101.9, 31.45) * mm});
            skLineSegment(sketch, "E318", {"start": v(-101.9, 31.45) * mm, "end": v(-101.9, 44.75) * mm});
            skLineSegment(sketch, "E319", {"start": v(-82.85, 44.75) * mm, "end": v(-69.55, 44.75) * mm});
            skLineSegment(sketch, "E320", {"start": v(-69.55, 44.75) * mm, "end": v(-69.55, 31.45) * mm});
            skLineSegment(sketch, "E321", {"start": v(-69.55, 31.45) * mm, "end": v(-82.85, 31.45) * mm});
            skLineSegment(sketch, "E322", {"start": v(-82.85, 31.45) * mm, "end": v(-82.85, 44.75) * mm});
            skLineSegment(sketch, "E323", {"start": v(-63.8, 44.75) * mm, "end": v(-50.5, 44.75) * mm});
            skLineSegment(sketch, "E324", {"start": v(-50.5, 44.75) * mm, "end": v(-50.5, 31.45) * mm});
            skLineSegment(sketch, "E325", {"start": v(-50.5, 31.45) * mm, "end": v(-63.8, 31.45) * mm});
            skLineSegment(sketch, "E326", {"start": v(-63.8, 31.45) * mm, "end": v(-63.8, 44.75) * mm});
            skLineSegment(sketch, "E327", {"start": v(-44.75, 44.75) * mm, "end": v(-31.45, 44.75) * mm});
            skLineSegment(sketch, "E328", {"start": v(-31.45, 44.75) * mm, "end": v(-31.45, 31.45) * mm});
            skLineSegment(sketch, "E329", {"start": v(-31.45, 31.45) * mm, "end": v(-44.75, 31.45) * mm});
            skLineSegment(sketch, "E330", {"start": v(-44.75, 31.45) * mm, "end": v(-44.75, 44.75) * mm});
            skLineSegment(sketch, "E331", {"start": v(-25.7, 44.75) * mm, "end": v(-12.4, 44.75) * mm});
            skLineSegment(sketch, "E332", {"start": v(-12.4, 44.75) * mm, "end": v(-12.4, 31.45) * mm});
            skLineSegment(sketch, "E333", {"start": v(-12.4, 31.45) * mm, "end": v(-25.7, 31.45) * mm});
            skLineSegment(sketch, "E334", {"start": v(-25.7, 31.45) * mm, "end": v(-25.7, 44.75) * mm});
            skLineSegment(sketch, "E335", {"start": v(-6.65, 44.75) * mm, "end": v(6.65, 44.75) * mm});
            skLineSegment(sketch, "E336", {"start": v(6.65, 44.75) * mm, "end": v(6.65, 31.45) * mm});
            skLineSegment(sketch, "E337", {"start": v(6.65, 31.45) * mm, "end": v(-6.65, 31.45) * mm});
            skLineSegment(sketch, "E338", {"start": v(-6.65, 31.45) * mm, "end": v(-6.65, 44.75) * mm});
            skLineSegment(sketch, "E339", {"start": v(12.4, 44.75) * mm, "end": v(25.7, 44.75) * mm});
            skLineSegment(sketch, "E340", {"start": v(25.7, 44.75) * mm, "end": v(25.7, 31.45) * mm});
            skLineSegment(sketch, "E341", {"start": v(25.7, 31.45) * mm, "end": v(12.4, 31.45) * mm});
            skLineSegment(sketch, "E342", {"start": v(12.4, 31.45) * mm, "end": v(12.4, 44.75) * mm});
            skLineSegment(sketch, "E343", {"start": v(31.45, 44.75) * mm, "end": v(44.75, 44.75) * mm});
            skLineSegment(sketch, "E344", {"start": v(44.75, 44.75) * mm, "end": v(44.75, 31.45) * mm});
            skLineSegment(sketch, "E345", {"start": v(44.75, 31.45) * mm, "end": v(31.45, 31.45) * mm});
            skLineSegment(sketch, "E346", {"start": v(31.45, 31.45) * mm, "end": v(31.45, 44.75) * mm});
            skLineSegment(sketch, "E347", {"start": v(50.5, 44.75) * mm, "end": v(63.8, 44.75) * mm});
            skLineSegment(sketch, "E348", {"start": v(63.8, 44.75) * mm, "end": v(63.8, 31.45) * mm});
            skLineSegment(sketch, "E349", {"start": v(63.8, 31.45) * mm, "end": v(50.5, 31.45) * mm});
            skLineSegment(sketch, "E350", {"start": v(50.5, 31.45) * mm, "end": v(50.5, 44.75) * mm});
            skLineSegment(sketch, "E351", {"start": v(69.55, 44.75) * mm, "end": v(82.85, 44.75) * mm});
            skLineSegment(sketch, "E352", {"start": v(82.85, 44.75) * mm, "end": v(82.85, 31.45) * mm});
            skLineSegment(sketch, "E353", {"start": v(82.85, 31.45) * mm, "end": v(69.55, 31.45) * mm});
            skLineSegment(sketch, "E354", {"start": v(69.55, 31.45) * mm, "end": v(69.55, 44.75) * mm});
            skLineSegment(sketch, "E355", {"start": v(88.6, 44.75) * mm, "end": v(101.9, 44.75) * mm});
            skLineSegment(sketch, "E356", {"start": v(101.9, 44.75) * mm, "end": v(101.9, 31.45) * mm});
            skLineSegment(sketch, "E357", {"start": v(101.9, 31.45) * mm, "end": v(88.6, 31.45) * mm});
            skLineSegment(sketch, "E358", {"start": v(88.6, 31.45) * mm, "end": v(88.6, 44.75) * mm});
            skLineSegment(sketch, "E359.top", {"start": v(-6.65, -44.75) * mm, "end": v(-5.26, -44.75) * mm});
            skLineSegment(sketch, "E359.left", {"start": v(-6.65, -31.45) * mm, "end": v(-6.65, -36.15) * mm});
            skPoint(sketch, "E359.middle", {"position": v(0, -38.1) * mm});
            skLineSegment(sketch, "E360", {"start": v(6.65, -31.45) * mm, "end": v(6.65, -36.15) * mm});
            skLineSegment(sketch, "E361", {"start": v(-18.56, -36.15) * mm, "end": v(-6.65, -36.15) * mm});
            skLineSegment(sketch, "E362", {"start": v(-18.56, -40.05) * mm, "end": v(-6.65, -40.05) * mm});
            skLineSegment(sketch, "E363.trimOffspring", {"start": v(-6.65, -40.05) * mm, "end": v(-6.65, -44.75) * mm});
            skLineSegment(sketch, "E364.trimOffspring", {"start": v(6.65, -40.05) * mm, "end": v(6.65, -44.75) * mm});
            skLineSegment(sketch, "E365", {"start": v(-5.26, -31.45) * mm, "end": v(6.65, -31.45) * mm});
            skLineSegment(sketch, "E366", {"start": v(-5.26, -44.75) * mm, "end": v(6.65, -44.75) * mm});
            skSolve(sketch);
        }
        {
            var Q0;
            Q0 = qSketchRegion(id + "F2", true);
            extrude(context, id + "F3", {"entities" : qUnion([Q0]), "operationType" : NewBodyOperationType.REMOVE, "endBound" : BoundingType.THROUGH_ALL, "oppositeDirection" : true, "depth" : 25 * mm});
        }
    });
